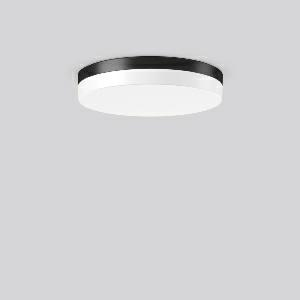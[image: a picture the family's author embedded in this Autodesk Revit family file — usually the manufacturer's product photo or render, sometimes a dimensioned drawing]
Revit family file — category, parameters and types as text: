
# Revit family: flat_slim_round_312631_0031_19_f120
name_source: partatom
category: Lighting Fixtures
units: mm (PartAtom-declared; Revit-internal decimal feet)

## family parameters
Cut with Voids When Loaded = No
Host = Face
Light Source = No
Part Type = Normal
Room Calculation Point = No
Round Connector Dimension = Use Diameter
Shared = No

## types (1)
- MultiLumen 1 830 (1 x LED Modul 830, 2450 lm, 3000)
    Apparent Load = 25 VA
    CIE Flux Codes = 40 70 90 84 100
    Color Rendering = 80
    Color Temperature = 3000
    Default Elevation = 1800 mm
    Height = 75 mm
    Lamp = 1 x LED Modul 830
    Lamp Light Flux = 2450 lm
    Lamp count = 1
    Length = 400 mm
    Lifetime = 50000 h
    Luminous efficacy = 98 lm/W
    Manufacturer = RZB
    ModVariant = No
    Model = 312631.0031.19
    Mounting Place = Ceiling
    Mounting Type = Surface mounted
    Number of Poles = 1
    OnlyDefault = Yes
    Power Factor = 1
    Product Name = FLAT SLIM round
    Product group = Surface mounted ceiling and wall luminaires
    ProductGroupID = 305
    Protection Class = Protection class I
    Protection Degree = Degree of protection
    RLX_Detail_Level = 1
    RLX_Emergency_Light_Flux = 0 lm
    RLX_Emergency_Type = 0
    RLX_Emergency_Type_DB = No
    RlxData = <blob elided: 21997 chars, md5=142f41ea>
    Socket = socket
    Standby Power = 0 W
    System Light Flux = 2450 lm
    System Power = 25 W
    Type Comments = MultiLumen 1 830
    Type Image = 312631.0031.jpg
    URL = http://relux.com
    VarID = multilumen_1_830
    Voltage = 0 V
    Weight = 0.00 kg
    Width = 0 mm  [stored 0 ft]

note: [stored X ft] marks values corroborated as IEEE doubles in the binary element streams (Revit-internal decimal feet)

## geometry (parser evidence)
native form markers: Blend x4, Sweep x12
no freeform markers — native parametric forms only
